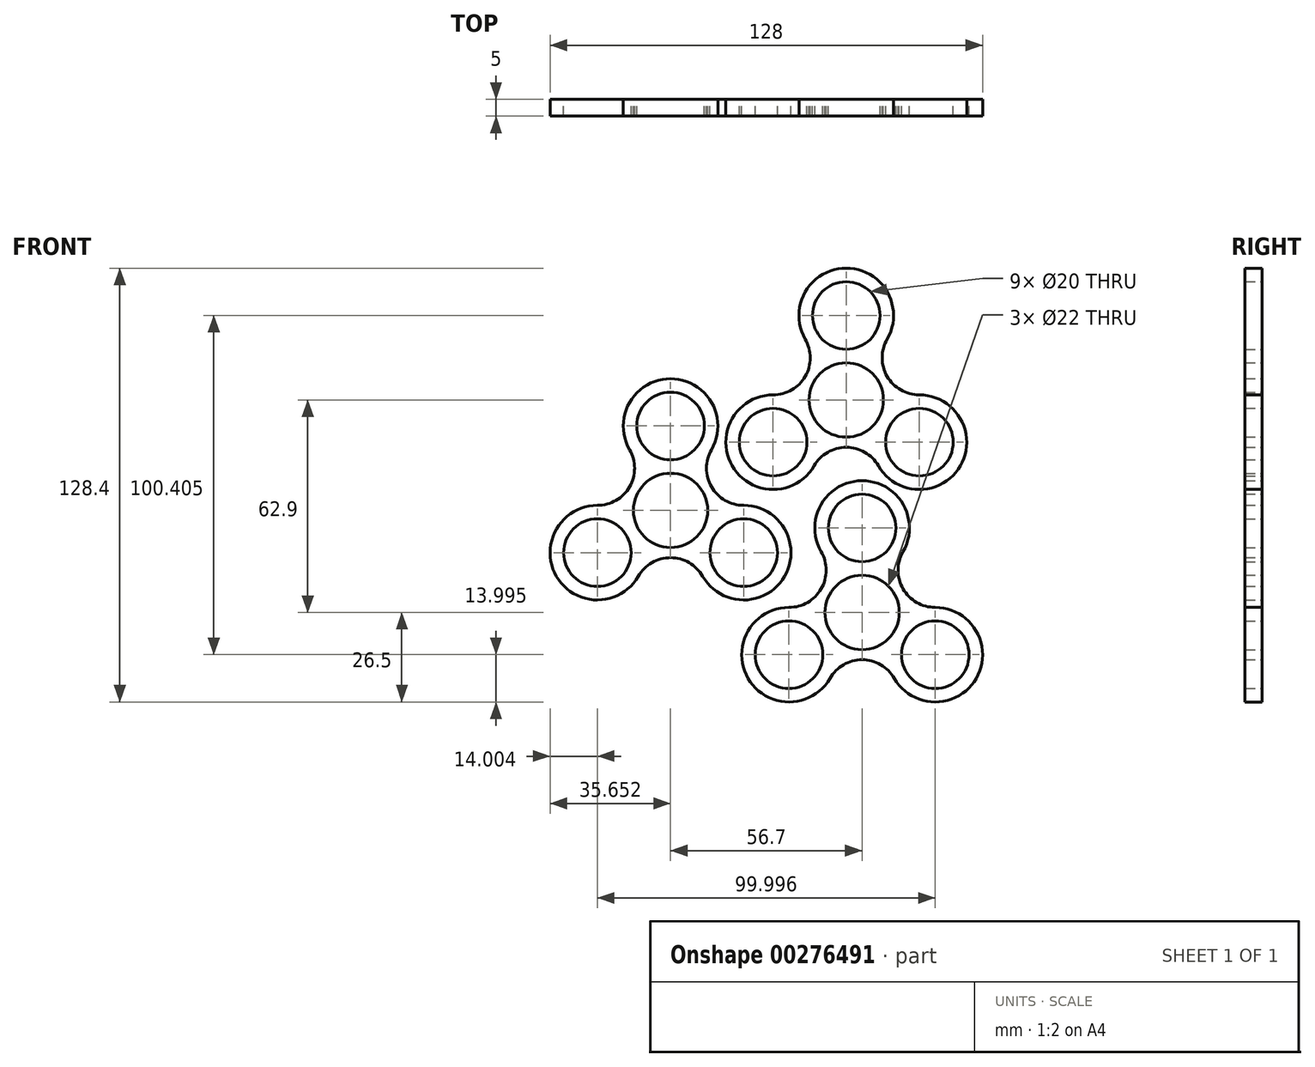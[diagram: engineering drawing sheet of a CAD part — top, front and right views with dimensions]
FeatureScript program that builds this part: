
annotation { "Feature Type Name" : "Feature", "Feature Type Description" : "" }
export const myFeature = defineFeature(function(context is Context, id is Id, definition is map)
    precondition{}
    {
        {
            var Q0;
            Q0=qCreatedBy(makeId("Front.planeOp"),FACE);
            var sketch = newSketch(context, id + "F0", { "sketchPlane" : qUnion([Q0])});
            skCircle(sketch, "E0", {"center": v(16.93, -40.24) * mm, "radius": 39 * mm});
            skCircle(sketch, "E1", {"center": v(16.93, -40.24) * mm, "radius": 11 * mm});
            skArc(sketch, "E2", {"start": v(16.93, -1.24) * mm, "mid": v(-16.84, -20.74) * mm, "end": v(-16.84, -59.75) * mm});
            skArc(sketch, "E3", {"start": v(-16.84, -59.75) * mm, "mid": v(16.93, -79.25) * mm, "end": v(50.7, -59.75) * mm});
            skLineSegment(sketch, "E4", {"start": v(-16.84, -59.75) * mm, "end": v(-13.37, -57.75) * mm});
            skLineSegment(sketch, "E5", {"start": v(16.93, -1.24) * mm, "end": v(16.93, -5.24) * mm});
            skLineSegment(sketch, "E6", {"start": v(50.7, -59.75) * mm, "end": v(47.24, -57.75) * mm});
            skCircle(sketch, "E7", {"center": v(16.93, -15.24) * mm, "radius": 10 * mm});
            skCircle(sketch, "E8", {"center": v(-4.72, -52.74) * mm, "radius": 10 * mm});
            skCircle(sketch, "E9", {"center": v(38.58, -52.74) * mm, "radius": 10 * mm});
            skCircle(sketch, "E10", {"center": v(16.93, -15.24) * mm, "radius": 14 * mm});
            skCircle(sketch, "E11", {"center": v(-4.72, -52.74) * mm, "radius": 14 * mm});
            skCircle(sketch, "E12", {"center": v(38.58, -52.74) * mm, "radius": 14 * mm});
            skPoint(sketch, "E13", {"position": v(16.93, -54.24) * mm});
            skPoint(sketch, "E14", {"position": v(4.6, -33.6) * mm});
            skPoint(sketch, "E15", {"position": v(28.85, -32.89) * mm});
            skArc(sketch, "E16", {"start": v(29.05, -22.25) * mm, "mid": v(29.05, -33.25) * mm, "end": v(38.57, -38.74) * mm});
            skArc(sketch, "E17", {"start": v(-4.7, -38.74) * mm, "mid": v(4.82, -33.25) * mm, "end": v(4.81, -22.25) * mm});
            skArc(sketch, "E18", {"start": v(26.45, -59.74) * mm, "mid": v(16.93, -54.24) * mm, "end": v(7.41, -59.74) * mm});
            skSolve(sketch);
        }
        {
            var Q0;
            {var subQ5=sQuery(id+"F0.wireOp",EDGE,"E16");Q0=makeQuery(id+"F0.imprint","IMPRINT",FACE,{"disambiguationData":[TD([[makeQuery(id+"F0.imprint","IMPRINT",EDGE,{"derivedFrom":subQ5}),-1.0]])]});}
            var Q1;
            Q1=makeQuery(id+"F0.imprint","IMPRINT",FACE,{"disambiguationData":[TD([[makeQuery(id+"F0.imprint","IMPRINT",EDGE,{"derivedFrom":sQuery(id+"F0.wireOp",EDGE,"E9")}),-1.0]])]});
            var Q2;
            {var subQ5=sQuery(id+"F0.wireOp",EDGE,"E18");Q2=makeQuery(id+"F0.imprint","IMPRINT",FACE,{"disambiguationData":[TD([[makeQuery(id+"F0.imprint","IMPRINT",EDGE,{"derivedFrom":subQ5}),-1.0]])]});}
            var Q3;
            Q3=makeQuery(id+"F0.imprint","IMPRINT",FACE,{"disambiguationData":[TD([[makeQuery(id+"F0.imprint","IMPRINT",EDGE,{"derivedFrom":sQuery(id+"F0.wireOp",EDGE,"E8")}),-1.0]])]});
            var Q4;
            {var subQ5=sQuery(id+"F0.wireOp",EDGE,"E17");Q4=makeQuery(id+"F0.imprint","IMPRINT",FACE,{"disambiguationData":[TD([[makeQuery(id+"F0.imprint","IMPRINT",EDGE,{"derivedFrom":subQ5}),-1.0]])]});}
            var Q5;
            Q5=makeQuery(id+"F0.imprint","IMPRINT",FACE,{"disambiguationData":[TD([[makeQuery(id+"F0.imprint","IMPRINT",EDGE,{"derivedFrom":sQuery(id+"F0.wireOp",EDGE,"E7")}),-1.0]])]});
            extrude(context, id + "F1", {"entities" : qUnion([Q0, Q1, Q2, Q3, Q4, Q5]), "depth" : 5 * mm});
        }
        {
            var Q0;
            Q0=qCreatedBy(makeId("Front.planeOp"),FACE);
            var sketch = newSketch(context, id + "F2", { "sketchPlane" : qUnion([Q0])});
            skLineSegment(sketch, "E19", {"start": v(-59.68, 64.11) * mm, "end": v(-59.68, -13.89) * mm});
            skLineSegment(sketch, "E20", {"start": v(-59.68, 64.11) * mm, "end": v(-59.68, 61.11) * mm});
            skLineSegment(sketch, "E21", {"start": v(-59.68, 61.11) * mm, "end": v(-59.68, 39.11) * mm});
            skLineSegment(sketch, "E22", {"start": v(-59.68, 39.11) * mm, "end": v(-59.68, 36.11) * mm});
            skLineSegment(sketch, "E23", {"start": v(-59.68, 36.11) * mm, "end": v(-59.68, 14.11) * mm});
            skLineSegment(sketch, "E24", {"start": v(-59.68, 14.11) * mm, "end": v(-59.68, 11.11) * mm});
            skLineSegment(sketch, "E25", {"start": v(-59.68, 11.11) * mm, "end": v(-59.68, -10.89) * mm});
            skLineSegment(sketch, "E26", {"start": v(-59.68, -10.89) * mm, "end": v(-59.68, -13.89) * mm});
            skCircle(sketch, "E27", {"center": v(-59.68, 50.11) * mm, "radius": 11 * mm});
            skCircle(sketch, "E28", {"center": v(-59.68, 25.11) * mm, "radius": 11 * mm});
            skCircle(sketch, "E29", {"center": v(-59.68, 0.11) * mm, "radius": 11 * mm});
            skCircle(sketch, "E30", {"center": v(-59.68, 0.11) * mm, "radius": 14 * mm});
            skCircle(sketch, "E31", {"center": v(-59.68, 25.11) * mm, "radius": 14 * mm});
            skCircle(sketch, "E32", {"center": v(-59.68, 50.11) * mm, "radius": 14 * mm});
            skArc(sketch, "E33", {"start": v(-48.31, 16.94) * mm, "mid": v(-49.7, 12.61) * mm, "end": v(-48.31, 8.28) * mm});
            skArc(sketch, "E34.MirrorCS", {"start": v(-71.05, 16.94) * mm, "mid": v(-69.66, 12.61) * mm, "end": v(-71.05, 8.28) * mm});
            skLineSegment(sketch, "E35", {"start": v(-70.68, 25.11) * mm, "end": v(-48.68, 25.11) * mm});
            skArc(sketch, "E36.MirrorCS", {"start": v(-48.31, 33.28) * mm, "mid": v(-49.7, 37.61) * mm, "end": v(-48.31, 41.94) * mm});
            skArc(sketch, "E37.MirrorCS", {"start": v(-71.05, 33.28) * mm, "mid": v(-69.66, 37.61) * mm, "end": v(-71.05, 41.94) * mm});
            skSolve(sketch);
        }
        {
            var Q0;
            {var subQ7=sQuery(id+"F2.wireOp",EDGE,"E20");Q0=makeQuery(id+"F2.imprint","IMPRINT",FACE,{"disambiguationData":[TD([[makeQuery(id+"F2.imprint","IMPRINT",EDGE,{"derivedFrom":subQ7}),1.0]])]});}
            var Q1;
            {var subQ0=sQuery(id+"F2.wireOp",EDGE,"E37.MirrorCS");Q1=makeQuery(id+"F2.imprint","IMPRINT",FACE,{"disambiguationData":[TD([[makeQuery(id+"F2.imprint","IMPRINT",EDGE,{"derivedFrom":subQ0}),-1.0]])]});}
            var Q2;
            {var subQ1=sQuery(id+"F2.wireOp",EDGE,"E20");Q2=makeQuery(id+"F2.imprint","IMPRINT",FACE,{"disambiguationData":[TD([[makeQuery(id+"F2.imprint","IMPRINT",EDGE,{"derivedFrom":subQ1}),-1.0]])]});}
            var Q3;
            {var subQ0=sQuery(id+"F2.wireOp",EDGE,"E22");Q3=makeQuery(id+"F2.imprint","IMPRINT",FACE,{"disambiguationData":[TD([[makeQuery(id+"F2.imprint","IMPRINT",EDGE,{"derivedFrom":subQ0}),-1.0]])]});}
            var Q4;
            {var subQ0=sQuery(id+"F2.wireOp",EDGE,"E22");Q4=makeQuery(id+"F2.imprint","IMPRINT",FACE,{"disambiguationData":[TD([[makeQuery(id+"F2.imprint","IMPRINT",EDGE,{"derivedFrom":subQ0}),1.0]])]});}
            var Q5;
            {var subQ0=sQuery(id+"F2.wireOp",EDGE,"E31");var subQ1=makeQuery(id+"F2.imprint","INTERSECT",VERTEX,{"derivedFrom":[subQ0,sQuery(id+"F2.wireOp",EDGE,"E36.MirrorCS")]});Q5=makeQuery(id+"F2.imprint","IMPRINT",FACE,{"disambiguationData":[TD([[makeQuery(id+"F2.imprint","IMPRINT",EDGE,{"disambiguationData":[TD([[subQ1,-1.0]])],"derivedFrom":subQ0}),1.0]])]});}
            var Q6;
            {var subQ0=sQuery(id+"F2.wireOp",EDGE,"E36.MirrorCS");Q6=makeQuery(id+"F2.imprint","IMPRINT",FACE,{"disambiguationData":[TD([[makeQuery(id+"F2.imprint","IMPRINT",EDGE,{"derivedFrom":subQ0}),1.0]])]});}
            var Q7;
            {var subQ0=sQuery(id+"F2.wireOp",EDGE,"E31");var subQ1=makeQuery(id+"F2.imprint","INTERSECT",VERTEX,{"derivedFrom":[subQ0,sQuery(id+"F2.wireOp",EDGE,"E37.MirrorCS")]});Q7=makeQuery(id+"F2.imprint","IMPRINT",FACE,{"disambiguationData":[TD([[makeQuery(id+"F2.imprint","IMPRINT",EDGE,{"disambiguationData":[TD([[subQ1,1.0]])],"derivedFrom":subQ0}),1.0]])]});}
            var Q8;
            {var subQ0=sQuery(id+"F2.wireOp",EDGE,"E24");Q8=makeQuery(id+"F2.imprint","IMPRINT",FACE,{"disambiguationData":[TD([[makeQuery(id+"F2.imprint","IMPRINT",EDGE,{"derivedFrom":subQ0}),-1.0]])]});}
            var Q9;
            {var subQ0=sQuery(id+"F2.wireOp",EDGE,"E24");Q9=makeQuery(id+"F2.imprint","IMPRINT",FACE,{"disambiguationData":[TD([[makeQuery(id+"F2.imprint","IMPRINT",EDGE,{"derivedFrom":subQ0}),1.0]])]});}
            var Q10;
            {var subQ0=sQuery(id+"F2.wireOp",EDGE,"E33");Q10=makeQuery(id+"F2.imprint","IMPRINT",FACE,{"disambiguationData":[TD([[makeQuery(id+"F2.imprint","IMPRINT",EDGE,{"derivedFrom":subQ0}),-1.0]])]});}
            var Q11;
            {var subQ1=sQuery(id+"F2.wireOp",EDGE,"E26");Q11=makeQuery(id+"F2.imprint","IMPRINT",FACE,{"disambiguationData":[TD([[makeQuery(id+"F2.imprint","IMPRINT",EDGE,{"derivedFrom":subQ1}),1.0]])]});}
            var Q12;
            {var subQ0=sQuery(id+"F2.wireOp",EDGE,"E34.MirrorCS");Q12=makeQuery(id+"F2.imprint","IMPRINT",FACE,{"disambiguationData":[TD([[makeQuery(id+"F2.imprint","IMPRINT",EDGE,{"derivedFrom":subQ0}),1.0]])]});}
            var Q13;
            {var subQ1=sQuery(id+"F2.wireOp",EDGE,"E26");Q13=makeQuery(id+"F2.imprint","IMPRINT",FACE,{"disambiguationData":[TD([[makeQuery(id+"F2.imprint","IMPRINT",EDGE,{"derivedFrom":subQ1}),-1.0]])]});}
            extrude(context, id + "F3", {"entities" : qUnion([Q0, Q1, Q2, Q3, Q4, Q5, Q6, Q7, Q8, Q9, Q10, Q11, Q12, Q13]), "depth" : 5 * mm});
        }
        {
            var Q0;
            Q0=makeQuery(id+"F3.opExtrude","CAP_EDGE",EDGE,{"disambiguationData":[OSD([sQuery(id+"F2.wireOp",EDGE,"E32")])],"isStart":false});
            var Q1;
            Q1=makeQuery(id+"F3.opExtrude","CAP_EDGE",EDGE,{"disambiguationData":[OSD([sQuery(id+"F2.wireOp",EDGE,"E37.MirrorCS")])],"isStart":false});
            var Q2;
            {var subQ0=sQuery(id+"F2.wireOp",EDGE,"E31");Q2=makeQuery(id+"F3.opExtrude","CAP_EDGE",EDGE,{"disambiguationData":[OSD([subQ0]),TDD([makeQuery(id+"F2.imprint","IMPRINT",EDGE,{"disambiguationData":[TD([[makeQuery(id+"F2.imprint","INTERSECT",VERTEX,{"derivedFrom":[subQ0,sQuery(id+"F2.wireOp",EDGE,"E34.MirrorCS")]}),1.0]])],"derivedFrom":subQ0})])],"isStart":false});}
            var Q3;
            Q3=makeQuery(id+"F3.opExtrude","CAP_EDGE",EDGE,{"disambiguationData":[OSD([sQuery(id+"F2.wireOp",EDGE,"E32")])],"isStart":true});
            var Q4;
            {var subQ0=sQuery(id+"F2.wireOp",EDGE,"E31");Q4=makeQuery(id+"F3.opExtrude","CAP_EDGE",EDGE,{"disambiguationData":[OSD([subQ0]),TDD([makeQuery(id+"F2.imprint","IMPRINT",EDGE,{"disambiguationData":[TD([[makeQuery(id+"F2.imprint","INTERSECT",VERTEX,{"derivedFrom":[subQ0,sQuery(id+"F2.wireOp",EDGE,"E33")]}),-1.0]])],"derivedFrom":subQ0})])],"isStart":true});}
            var Q5;
            Q5=makeQuery(id+"F3.opExtrude","CAP_EDGE",EDGE,{"disambiguationData":[OSD([sQuery(id+"F2.wireOp",EDGE,"E33")])],"isStart":true});
            var Q6;
            Q6=makeQuery(id+"F3.opExtrude","CAP_EDGE",EDGE,{"disambiguationData":[OSD([sQuery(id+"F2.wireOp",EDGE,"E30")])],"isStart":true});
            var Q7;
            Q7=makeQuery(id+"F3.opExtrude","CAP_EDGE",EDGE,{"disambiguationData":[OSD([sQuery(id+"F2.wireOp",EDGE,"E34.MirrorCS")])],"isStart":true});
            var Q8;
            {var subQ0=sQuery(id+"F2.wireOp",EDGE,"E31");Q8=makeQuery(id+"F3.opExtrude","CAP_EDGE",EDGE,{"disambiguationData":[OSD([subQ0]),TDD([makeQuery(id+"F2.imprint","IMPRINT",EDGE,{"disambiguationData":[TD([[makeQuery(id+"F2.imprint","INTERSECT",VERTEX,{"derivedFrom":[subQ0,sQuery(id+"F2.wireOp",EDGE,"E34.MirrorCS")]}),1.0]])],"derivedFrom":subQ0})])],"isStart":true});}
            var Q9;
            Q9=makeQuery(id+"F3.opExtrude","CAP_EDGE",EDGE,{"disambiguationData":[OSD([sQuery(id+"F2.wireOp",EDGE,"E37.MirrorCS")])],"isStart":true});
            var Q10;
            Q10=makeQuery(id+"F3.opExtrude","CAP_EDGE",EDGE,{"disambiguationData":[OSD([sQuery(id+"F2.wireOp",EDGE,"E36.MirrorCS")])],"isStart":true});
            var Q11;
            Q11=makeQuery(id+"F3.opExtrude","CAP_EDGE",EDGE,{"disambiguationData":[OSD([sQuery(id+"F2.wireOp",EDGE,"E36.MirrorCS")])],"isStart":false});
            var Q12;
            {var subQ0=sQuery(id+"F2.wireOp",EDGE,"E31");Q12=makeQuery(id+"F3.opExtrude","CAP_EDGE",EDGE,{"disambiguationData":[OSD([subQ0]),TDD([makeQuery(id+"F2.imprint","IMPRINT",EDGE,{"disambiguationData":[TD([[makeQuery(id+"F2.imprint","INTERSECT",VERTEX,{"derivedFrom":[subQ0,sQuery(id+"F2.wireOp",EDGE,"E33")]}),-1.0]])],"derivedFrom":subQ0})])],"isStart":false});}
            var Q13;
            Q13=makeQuery(id+"F3.opExtrude","CAP_EDGE",EDGE,{"disambiguationData":[OSD([sQuery(id+"F2.wireOp",EDGE,"E33")])],"isStart":false});
            var Q14;
            Q14=makeQuery(id+"F3.opExtrude","CAP_EDGE",EDGE,{"disambiguationData":[OSD([sQuery(id+"F2.wireOp",EDGE,"E30")])],"isStart":false});
            var Q15;
            Q15=makeQuery(id+"F3.opExtrude","CAP_EDGE",EDGE,{"disambiguationData":[OSD([sQuery(id+"F2.wireOp",EDGE,"E34.MirrorCS")])],"isStart":false});
            fillet(context, id + "F4", {"entities" : qUnion([Q0, Q1, Q2, Q3, Q4, Q5, Q6, Q7, Q8, Q9, Q10, Q11, Q12, Q13, Q14, Q15]), "radius" : 2.5 * mm, "tangentPropagation" : true, "allowEdgeOverflow" : false});
        }
        {
            var Q0;
            Q0=makeQuery(id+"F1.opExtrude","SWEPT_BODY",BODY,{"disambiguationData":[OSD([sQuery(id+"F0.wireOp",EDGE,"E1"),sQuery(id+"F0.wireOp",EDGE,"E7"),sQuery(id+"F0.wireOp",EDGE,"E8"),sQuery(id+"F0.wireOp",EDGE,"E9"),sQuery(id+"F0.wireOp",EDGE,"E10"),sQuery(id+"F0.wireOp",EDGE,"E11"),sQuery(id+"F0.wireOp",EDGE,"E12"),sQuery(id+"F0.wireOp",EDGE,"E16"),sQuery(id+"F0.wireOp",EDGE,"E17"),sQuery(id+"F0.wireOp",EDGE,"E18")])]});
            transform(context, id + "F5", {"entities" : qUnion([Q0]), "transformType" : TransformType.TRANSLATION_3D, "dx" : -4.7 * mm, "dy" : 0 * mm, "dz" : 62.9 * mm, "makeCopy" : true});
        }
        {
            var Q0;
            Q0=makeQuery(id+"F5.opPattern","COPY",BODY,{"derivedFrom":makeQuery(id+"F1.opExtrude","SWEPT_BODY",BODY,{"disambiguationData":[OSD([sQuery(id+"F0.wireOp",EDGE,"E1"),sQuery(id+"F0.wireOp",EDGE,"E7"),sQuery(id+"F0.wireOp",EDGE,"E8"),sQuery(id+"F0.wireOp",EDGE,"E9"),sQuery(id+"F0.wireOp",EDGE,"E10"),sQuery(id+"F0.wireOp",EDGE,"E11"),sQuery(id+"F0.wireOp",EDGE,"E12"),sQuery(id+"F0.wireOp",EDGE,"E16"),sQuery(id+"F0.wireOp",EDGE,"E17"),sQuery(id+"F0.wireOp",EDGE,"E18")])]}),"instanceName":"1"});
            transform(context, id + "F6", {"entities" : qUnion([Q0]), "transformType" : TransformType.TRANSLATION_3D, "dx" : -52 * mm, "dy" : 0 * mm, "dz" : -32.7 * mm, "makeCopy" : true});
        }
        {
            var Q0;
            Q0=makeQuery(id+"F3.opExtrude","SWEPT_BODY",BODY,{"disambiguationData":[OSD([sQuery(id+"F2.wireOp",EDGE,"E27"),sQuery(id+"F2.wireOp",EDGE,"E28"),sQuery(id+"F2.wireOp",EDGE,"E29"),sQuery(id+"F2.wireOp",EDGE,"E30"),sQuery(id+"F2.wireOp",EDGE,"E31"),sQuery(id+"F2.wireOp",EDGE,"E32"),sQuery(id+"F2.wireOp",EDGE,"E33"),sQuery(id+"F2.wireOp",EDGE,"E34.MirrorCS"),sQuery(id+"F2.wireOp",EDGE,"E36.MirrorCS"),sQuery(id+"F2.wireOp",EDGE,"E37.MirrorCS")])]});
            deleteBodies(context, id + "F7", {"entities" : qUnion([Q0])});
        }
    });
